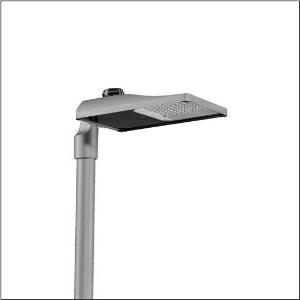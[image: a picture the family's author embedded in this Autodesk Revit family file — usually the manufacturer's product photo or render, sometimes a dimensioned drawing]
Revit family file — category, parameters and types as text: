
# Revit family: streetlight_sl_31_midi___pl52_5xh7h75n08la_2e4f
name_source: partatom
category: Lighting Fixtures
units: mm (PartAtom-declared; Revit-internal decimal feet)

## family parameters
Cut with Voids When Loaded = No
Host = Face
Light Source = No
Part Type = Normal
Room Calculation Point = No
Round Connector Dimension = Use Diameter
Shared = No

## types (1)
- --- (1 x LED, 10680 lm, 86.6 W, 2200K)
    Apparent Load = 87 VA
    CIE Flux Codes = 27 59 98 100 100
    Color Rendering = 70
    Color Temperature = 2200K
    Default Elevation = 1800 mm
    Description = Streetlight SL 31 midi NEMA (7pin), Desk-Remote mast luminaire for post-top, side-entry; light control with lens of PMMA; light distribution: PL52, direct asymmetric distribution, for standard-compliant lighting for roads and squares; LED: luminous flux: 10.680lm, light colour: 722, colour temperature: 2200K; luminous efficacy: 123,3lm/W; control: pre-setting: linear dimming characteristic, flexible luminous flux parameterisation, time-dependent luminous flux control, constant luminous flux control, intelligent temperature release in ECG and LED module, overheat protection; luminaire housing, of diecast aluminium, Siteco® metallic grey (DB 702S), corrosivity category C5 high according to DIN EN ISO 12944; cover of toughened safety glass, transparent, opened without tools; mast flange of diecast aluminium, Siteco® metallic grey (DB 702S), spigot size: 76/60mm, mast flange included unmounted; with cable H07RN-F 3x 1.5mm², cable length: 10,5m, connection cable pre-assembled; mains connection: 220..240V, AC, 50/60Hz; power consumption (at start of service life): 86,6W / (at end of service life): 90W / (with reduced operation 50%): 39,8W; protection rating (complete): IP66; insulation class (complete): insulation class I (protective earthing); impact resistance: IK10; certification: CE, ENEC, ENEC+, VDE, UKCA; permissible operating ambient temperature for outdoor applications: -40..+50°C; packaging unit: 1 piece

Light Distribution: PL52
    Height = 79 mm
    Lamp = 1 x LED
    Lamp Light Flux = 10680 lm
    Lamp Power = 86.6 W
    Lamp count = 1
    Length = 577 mm
    Luminous efficacy = 123 lm/W
    Manufacturer = Siteco
    ModVariant = No
    Model = 5XH7H75N08LA
    Number of Poles = 1
    OnlyDefault = Yes
    Power Factor = 1
    Product Name = Streetlight SL 31 midi | PL52
    Product group = mast luminaire | pylon top
    ProductGroupID = 6100
    Protection Class = Protection class I
    Protection Degree = IP 66
    RLX_Detail_Level = 1
    RLX_Emergency_Light_Flux = 0 lm
    RLX_Emergency_Type = 0
    RLX_Emergency_Type_DB = No
    RlxData = <blob elided: 52473 chars, md5=469a3137>
    Socket = socket
    Standby Power = 0 W
    System Light Flux = 10680 lm
    System Power = 87 W
    Type Comments = factory setting: luminous flux: 100 % | dim-lin: 254 | 456 mA
    Type Image = l_1300282.jpg
    URL = http://relux.com
    VarID = @adj_057684
    Voltage = 0 V
    Weight = 0.00 kg
    Width = 362 mm

## geometry (parser evidence)
native form markers: Blend x4, Sweep x11
no freeform markers — native parametric forms only
